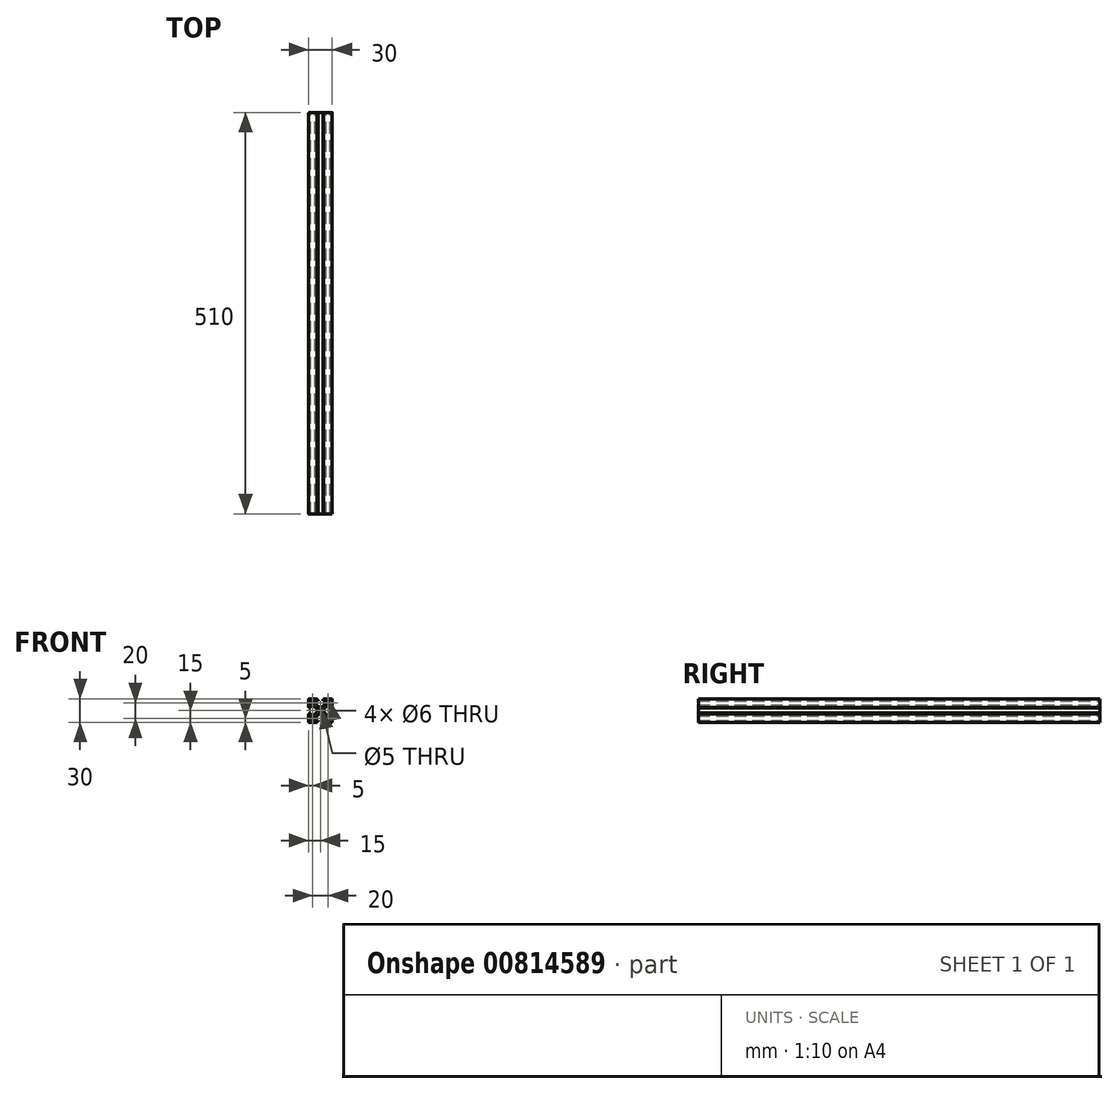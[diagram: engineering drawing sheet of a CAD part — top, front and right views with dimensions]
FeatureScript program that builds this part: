
annotation { "Feature Type Name" : "Feature", "Feature Type Description" : "" }
export const myFeature = defineFeature(function(context is Context, id is Id, definition is map)
    precondition{}
    {
        {
            var Q0;
            Q0=qCreatedBy(makeId("Front.planeOp"),FACE);
            var sketch = newSketch(context, id + "F0", { "sketchPlane" : qUnion([Q0])});
            skCircle(sketch, "E0", {"center": v(0, 0) * mm, "radius": 2.5 * mm});
            skCircle(sketch, "E1", {"center": v(-10, 10) * mm, "radius": 3 * mm});
            skCircle(sketch, "E2", {"center": v(10, 10) * mm, "radius": 3 * mm});
            skCircle(sketch, "E3", {"center": v(10, -10) * mm, "radius": 3 * mm});
            skCircle(sketch, "E4", {"center": v(-10, -10) * mm, "radius": 3 * mm});
            skLineSegment(sketch, "E5.bottom", {"start": v(-14, 15) * mm, "end": v(-4.5, 15) * mm});
            skLineSegment(sketch, "E5.top", {"start": v(-14, -15) * mm, "end": v(-4.2, -15) * mm});
            skLineSegment(sketch, "E5.left", {"start": v(-15, 14) * mm, "end": v(-15, 4.2) * mm});
            skLineSegment(sketch, "E5.right", {"start": v(15, 14) * mm, "end": v(15, 4.2) * mm});
            skPoint(sketch, "E6.visualSharp", {"position": v(-15, 15) * mm});
            skArc(sketch, "E6.filletArc", {"start": v(-14, 15) * mm, "mid": v(-14.7, 14.7) * mm, "end": v(-15, 14) * mm});
            skPoint(sketch, "E7.visualSharp", {"position": v(-15, -15) * mm});
            skArc(sketch, "E7.filletArc", {"start": v(-15, -14) * mm, "mid": v(-14.7, -14.7) * mm, "end": v(-14, -15) * mm});
            skPoint(sketch, "E8.visualSharp", {"position": v(15, -15) * mm});
            skArc(sketch, "E8.filletArc", {"start": v(14, -15) * mm, "mid": v(14.7, -14.7) * mm, "end": v(15, -14) * mm});
            skPoint(sketch, "E9.visualSharp", {"position": v(15, 15) * mm});
            skArc(sketch, "E9.filletArc", {"start": v(15, 14) * mm, "mid": v(14.7, 14.7) * mm, "end": v(14, 15) * mm});
            skLineSegment(sketch, "E10", {"start": v(-3.25, 13.7) * mm, "end": v(-3.25, 12.5) * mm});
            skLineSegment(sketch, "E11", {"start": v(-3.25, 12.5) * mm, "end": v(-5.25, 12.5) * mm});
            skLineSegment(sketch, "E12", {"start": v(-5.25, 12.5) * mm, "end": v(-5.25, 8) * mm});
            skLineSegment(sketch, "E13", {"start": v(-4.97, 7.3) * mm, "end": v(-2.54, 4.8) * mm});
            skLineSegment(sketch, "E14", {"start": v(-1.83, 4.5) * mm, "end": v(1.83, 4.5) * mm});
            skLineSegment(sketch, "E15", {"start": v(2.54, 4.8) * mm, "end": v(4.97, 7.3) * mm});
            skLineSegment(sketch, "E16", {"start": v(5.25, 8) * mm, "end": v(5.25, 12.5) * mm});
            skLineSegment(sketch, "E17", {"start": v(5.25, 12.5) * mm, "end": v(3.25, 12.5) * mm});
            skLineSegment(sketch, "E18", {"start": v(3.25, 12.5) * mm, "end": v(3.25, 13.7) * mm});
            skLineSegment(sketch, "E19.trimOffspring", {"start": v(4.5, 15) * mm, "end": v(14, 15) * mm});
            skPoint(sketch, "E20.visualSharp", {"position": v(-5.25, 7.6) * mm});
            skArc(sketch, "E20.filletArc", {"start": v(-5.25, 8) * mm, "mid": v(-5.18, 7.63) * mm, "end": v(-4.97, 7.3) * mm});
            skPoint(sketch, "E21.visualSharp", {"position": v(-2.25, 4.5) * mm});
            skArc(sketch, "E21.filletArc", {"start": v(-2.54, 4.8) * mm, "mid": v(-2.22, 4.58) * mm, "end": v(-1.83, 4.5) * mm});
            skPoint(sketch, "E22.visualSharp", {"position": v(2.25, 4.5) * mm});
            skArc(sketch, "E22.filletArc", {"start": v(1.83, 4.5) * mm, "mid": v(2.22, 4.58) * mm, "end": v(2.54, 4.8) * mm});
            skPoint(sketch, "E23.visualSharp", {"position": v(5.25, 7.6) * mm});
            skArc(sketch, "E23.filletArc", {"start": v(4.97, 7.3) * mm, "mid": v(5.18, 7.63) * mm, "end": v(5.25, 8) * mm});
            skLineSegment(sketch, "E24", {"start": v(-3.55, 14) * mm, "end": v(-3.7, 14) * mm});
            skLineSegment(sketch, "E25", {"start": v(-4.2, 14.5) * mm, "end": v(-4.2, 14.7) * mm});
            skLineSegment(sketch, "E26", {"start": v(3.55, 14) * mm, "end": v(3.7, 14) * mm});
            skLineSegment(sketch, "E27", {"start": v(4.2, 14.5) * mm, "end": v(4.2, 14.7) * mm});
            skPoint(sketch, "E28.visualSharp", {"position": v(-4.2, 15) * mm});
            skArc(sketch, "E28.filletArc", {"start": v(-4.2, 14.7) * mm, "mid": v(-4.29, 14.91) * mm, "end": v(-4.5, 15) * mm});
            skPoint(sketch, "E29.visualSharp", {"position": v(-3.25, 14) * mm});
            skArc(sketch, "E29.filletArc", {"start": v(-3.25, 13.7) * mm, "mid": v(-3.34, 13.91) * mm, "end": v(-3.55, 14) * mm});
            skPoint(sketch, "E30.visualSharp", {"position": v(3.25, 14) * mm});
            skArc(sketch, "E30.filletArc", {"start": v(3.55, 14) * mm, "mid": v(3.34, 13.91) * mm, "end": v(3.25, 13.7) * mm});
            skPoint(sketch, "E31.visualSharp", {"position": v(4.2, 15) * mm});
            skArc(sketch, "E31.filletArc", {"start": v(4.5, 15) * mm, "mid": v(4.29, 14.91) * mm, "end": v(4.2, 14.7) * mm});
            skPoint(sketch, "E32.visualSharp", {"position": v(4.2, 14) * mm});
            skArc(sketch, "E32.filletArc", {"start": v(3.7, 14) * mm, "mid": v(4.05, 14.15) * mm, "end": v(4.2, 14.5) * mm});
            skPoint(sketch, "E33.visualSharp", {"position": v(-4.2, 14) * mm});
            skArc(sketch, "E33.filletArc", {"start": v(-4.2, 14.5) * mm, "mid": v(-4.05, 14.15) * mm, "end": v(-3.7, 14) * mm});
            skPoint(sketch, "E34.1.0", {"position": v(-14, 3.25) * mm});
            skLineSegment(sketch, "E34.1.1", {"start": v(-12.5, -3.25) * mm, "end": v(-12.5, -5.25) * mm});
            skPoint(sketch, "E34.1.2", {"position": v(-15, 4.2) * mm});
            skPoint(sketch, "E34.1.3", {"position": v(-14, 4.2) * mm});
            skLineSegment(sketch, "E34.1.4", {"start": v(-12.5, -5.25) * mm, "end": v(-8, -5.25) * mm});
            skLineSegment(sketch, "E34.1.5", {"start": v(-4.8, 2.54) * mm, "end": v(-7.3, 4.97) * mm});
            skLineSegment(sketch, "E34.1.6", {"start": v(-12.5, 5.25) * mm, "end": v(-12.5, 3.25) * mm});
            skPoint(sketch, "E34.1.7", {"position": v(-15, -4.2) * mm});
            skPoint(sketch, "E34.1.8", {"position": v(-7.6, -5.25) * mm});
            skLineSegment(sketch, "E34.1.9", {"start": v(-8, 5.25) * mm, "end": v(-12.5, 5.25) * mm});
            skPoint(sketch, "E34.1.10", {"position": v(-14, -3.25) * mm});
            skPoint(sketch, "E34.1.11", {"position": v(-7.6, 5.25) * mm});
            skLineSegment(sketch, "E34.1.12", {"start": v(-4.5, -1.83) * mm, "end": v(-4.5, 1.83) * mm});
            skPoint(sketch, "E34.1.13", {"position": v(-4.5, 2.25) * mm});
            skPoint(sketch, "E34.1.14", {"position": v(-4.5, -2.25) * mm});
            skPoint(sketch, "E34.1.15", {"position": v(-14, -4.2) * mm});
            skLineSegment(sketch, "E34.1.16", {"start": v(-12.5, 3.25) * mm, "end": v(-13.7, 3.25) * mm});
            skLineSegment(sketch, "E34.1.17", {"start": v(-7.3, -4.97) * mm, "end": v(-4.8, -2.54) * mm});
            skLineSegment(sketch, "E34.1.18", {"start": v(-13.7, -3.25) * mm, "end": v(-12.5, -3.25) * mm});
            skArc(sketch, "E34.1.19", {"start": v(-14.5, -4.2) * mm, "mid": v(-14.15, -4.05) * mm, "end": v(-14, -3.7) * mm});
            skArc(sketch, "E34.1.20", {"start": v(-4.5, 1.83) * mm, "mid": v(-4.58, 2.22) * mm, "end": v(-4.8, 2.54) * mm});
            skArc(sketch, "E34.1.21", {"start": v(-8, -5.25) * mm, "mid": v(-7.63, -5.18) * mm, "end": v(-7.3, -4.97) * mm});
            skArc(sketch, "E34.1.22", {"start": v(-4.8, -2.54) * mm, "mid": v(-4.58, -2.22) * mm, "end": v(-4.5, -1.83) * mm});
            skArc(sketch, "E34.1.23", {"start": v(-7.3, 4.97) * mm, "mid": v(-7.63, 5.18) * mm, "end": v(-8, 5.25) * mm});
            skArc(sketch, "E34.1.24", {"start": v(-14, 3.55) * mm, "mid": v(-13.91, 3.34) * mm, "end": v(-13.7, 3.25) * mm});
            skLineSegment(sketch, "E34.1.25", {"start": v(-14, -3.55) * mm, "end": v(-14, -3.7) * mm});
            skArc(sketch, "E34.1.26", {"start": v(-14, 3.7) * mm, "mid": v(-14.15, 4.05) * mm, "end": v(-14.5, 4.2) * mm});
            skArc(sketch, "E34.1.27", {"start": v(-14.7, -4.2) * mm, "mid": v(-14.91, -4.29) * mm, "end": v(-15, -4.5) * mm});
            skArc(sketch, "E34.1.28", {"start": v(-13.7, -3.25) * mm, "mid": v(-13.91, -3.34) * mm, "end": v(-14, -3.55) * mm});
            skArc(sketch, "E34.1.29", {"start": v(-15, 4.5) * mm, "mid": v(-14.91, 4.29) * mm, "end": v(-14.7, 4.2) * mm});
            skLineSegment(sketch, "E34.1.30", {"start": v(-14.5, 4.2) * mm, "end": v(-14.7, 4.2) * mm});
            skLineSegment(sketch, "E34.1.31", {"start": v(-14.5, -4.2) * mm, "end": v(-14.7, -4.2) * mm});
            skLineSegment(sketch, "E34.1.32", {"start": v(-14, 3.55) * mm, "end": v(-14, 3.7) * mm});
            skPoint(sketch, "E34.2.0", {"position": v(-3.25, -14) * mm});
            skLineSegment(sketch, "E34.2.1", {"start": v(3.25, -12.5) * mm, "end": v(5.25, -12.5) * mm});
            skPoint(sketch, "E34.2.2", {"position": v(-4.2, -15) * mm});
            skPoint(sketch, "E34.2.3", {"position": v(-4.2, -14) * mm});
            skLineSegment(sketch, "E34.2.4", {"start": v(5.25, -12.5) * mm, "end": v(5.25, -8) * mm});
            skLineSegment(sketch, "E34.2.5", {"start": v(-2.54, -4.8) * mm, "end": v(-4.97, -7.3) * mm});
            skLineSegment(sketch, "E34.2.6", {"start": v(-5.25, -12.5) * mm, "end": v(-3.25, -12.5) * mm});
            skPoint(sketch, "E34.2.7", {"position": v(4.2, -15) * mm});
            skPoint(sketch, "E34.2.8", {"position": v(5.25, -7.6) * mm});
            skLineSegment(sketch, "E34.2.9", {"start": v(-5.25, -8) * mm, "end": v(-5.25, -12.5) * mm});
            skPoint(sketch, "E34.2.10", {"position": v(3.25, -14) * mm});
            skPoint(sketch, "E34.2.11", {"position": v(-5.25, -7.6) * mm});
            skLineSegment(sketch, "E34.2.12", {"start": v(1.83, -4.5) * mm, "end": v(-1.83, -4.5) * mm});
            skPoint(sketch, "E34.2.13", {"position": v(-2.25, -4.5) * mm});
            skPoint(sketch, "E34.2.14", {"position": v(2.25, -4.5) * mm});
            skPoint(sketch, "E34.2.15", {"position": v(4.2, -14) * mm});
            skLineSegment(sketch, "E34.2.16", {"start": v(-3.25, -12.5) * mm, "end": v(-3.25, -13.7) * mm});
            skLineSegment(sketch, "E34.2.17", {"start": v(4.97, -7.3) * mm, "end": v(2.54, -4.8) * mm});
            skLineSegment(sketch, "E34.2.18", {"start": v(3.25, -13.7) * mm, "end": v(3.25, -12.5) * mm});
            skArc(sketch, "E34.2.19", {"start": v(4.2, -14.5) * mm, "mid": v(4.05, -14.15) * mm, "end": v(3.7, -14) * mm});
            skArc(sketch, "E34.2.20", {"start": v(-1.83, -4.5) * mm, "mid": v(-2.22, -4.58) * mm, "end": v(-2.54, -4.8) * mm});
            skArc(sketch, "E34.2.21", {"start": v(5.25, -8) * mm, "mid": v(5.18, -7.63) * mm, "end": v(4.97, -7.3) * mm});
            skArc(sketch, "E34.2.22", {"start": v(2.54, -4.8) * mm, "mid": v(2.22, -4.58) * mm, "end": v(1.83, -4.5) * mm});
            skArc(sketch, "E34.2.23", {"start": v(-4.97, -7.3) * mm, "mid": v(-5.18, -7.63) * mm, "end": v(-5.25, -8) * mm});
            skArc(sketch, "E34.2.24", {"start": v(-3.55, -14) * mm, "mid": v(-3.34, -13.91) * mm, "end": v(-3.25, -13.7) * mm});
            skLineSegment(sketch, "E34.2.25", {"start": v(3.55, -14) * mm, "end": v(3.7, -14) * mm});
            skArc(sketch, "E34.2.26", {"start": v(-3.7, -14) * mm, "mid": v(-4.05, -14.15) * mm, "end": v(-4.2, -14.5) * mm});
            skArc(sketch, "E34.2.27", {"start": v(4.2, -14.7) * mm, "mid": v(4.29, -14.91) * mm, "end": v(4.5, -15) * mm});
            skArc(sketch, "E34.2.28", {"start": v(3.25, -13.7) * mm, "mid": v(3.34, -13.91) * mm, "end": v(3.55, -14) * mm});
            skArc(sketch, "E34.2.29", {"start": v(-4.5, -15) * mm, "mid": v(-4.29, -14.91) * mm, "end": v(-4.2, -14.7) * mm});
            skLineSegment(sketch, "E34.2.30", {"start": v(-4.2, -14.5) * mm, "end": v(-4.2, -14.7) * mm});
            skLineSegment(sketch, "E34.2.31", {"start": v(4.2, -14.5) * mm, "end": v(4.2, -14.7) * mm});
            skLineSegment(sketch, "E34.2.32", {"start": v(-3.55, -14) * mm, "end": v(-3.7, -14) * mm});
            skPoint(sketch, "E34.3.0", {"position": v(14, -3.25) * mm});
            skLineSegment(sketch, "E34.3.1", {"start": v(12.5, 3.25) * mm, "end": v(12.5, 5.25) * mm});
            skPoint(sketch, "E34.3.2", {"position": v(15, -4.2) * mm});
            skPoint(sketch, "E34.3.3", {"position": v(14, -4.2) * mm});
            skLineSegment(sketch, "E34.3.4", {"start": v(12.5, 5.25) * mm, "end": v(8, 5.25) * mm});
            skLineSegment(sketch, "E34.3.5", {"start": v(4.8, -2.54) * mm, "end": v(7.3, -4.97) * mm});
            skLineSegment(sketch, "E34.3.6", {"start": v(12.5, -5.25) * mm, "end": v(12.5, -3.25) * mm});
            skPoint(sketch, "E34.3.7", {"position": v(15, 4.2) * mm});
            skPoint(sketch, "E34.3.8", {"position": v(7.6, 5.25) * mm});
            skLineSegment(sketch, "E34.3.9", {"start": v(8, -5.25) * mm, "end": v(12.5, -5.25) * mm});
            skPoint(sketch, "E34.3.10", {"position": v(14, 3.25) * mm});
            skPoint(sketch, "E34.3.11", {"position": v(7.6, -5.25) * mm});
            skLineSegment(sketch, "E34.3.12", {"start": v(4.5, 1.83) * mm, "end": v(4.5, -1.83) * mm});
            skPoint(sketch, "E34.3.13", {"position": v(4.5, -2.25) * mm});
            skPoint(sketch, "E34.3.14", {"position": v(4.5, 2.25) * mm});
            skPoint(sketch, "E34.3.15", {"position": v(14, 4.2) * mm});
            skLineSegment(sketch, "E34.3.16", {"start": v(12.5, -3.25) * mm, "end": v(13.7, -3.25) * mm});
            skLineSegment(sketch, "E34.3.17", {"start": v(7.3, 4.97) * mm, "end": v(4.8, 2.54) * mm});
            skLineSegment(sketch, "E34.3.18", {"start": v(13.7, 3.25) * mm, "end": v(12.5, 3.25) * mm});
            skArc(sketch, "E34.3.19", {"start": v(14.5, 4.2) * mm, "mid": v(14.15, 4.05) * mm, "end": v(14, 3.7) * mm});
            skArc(sketch, "E34.3.20", {"start": v(4.5, -1.83) * mm, "mid": v(4.58, -2.22) * mm, "end": v(4.8, -2.54) * mm});
            skArc(sketch, "E34.3.21", {"start": v(8, 5.25) * mm, "mid": v(7.63, 5.18) * mm, "end": v(7.3, 4.97) * mm});
            skArc(sketch, "E34.3.22", {"start": v(4.8, 2.54) * mm, "mid": v(4.58, 2.22) * mm, "end": v(4.5, 1.83) * mm});
            skArc(sketch, "E34.3.23", {"start": v(7.3, -4.97) * mm, "mid": v(7.63, -5.18) * mm, "end": v(8, -5.25) * mm});
            skArc(sketch, "E34.3.24", {"start": v(14, -3.55) * mm, "mid": v(13.91, -3.34) * mm, "end": v(13.7, -3.25) * mm});
            skLineSegment(sketch, "E34.3.25", {"start": v(14, 3.55) * mm, "end": v(14, 3.7) * mm});
            skArc(sketch, "E34.3.26", {"start": v(14, -3.7) * mm, "mid": v(14.15, -4.05) * mm, "end": v(14.5, -4.2) * mm});
            skArc(sketch, "E34.3.27", {"start": v(14.7, 4.2) * mm, "mid": v(14.91, 4.29) * mm, "end": v(15, 4.5) * mm});
            skArc(sketch, "E34.3.28", {"start": v(13.7, 3.25) * mm, "mid": v(13.91, 3.34) * mm, "end": v(14, 3.55) * mm});
            skArc(sketch, "E34.3.29", {"start": v(15, -4.5) * mm, "mid": v(14.91, -4.29) * mm, "end": v(14.7, -4.2) * mm});
            skLineSegment(sketch, "E34.3.30", {"start": v(14.5, -4.2) * mm, "end": v(14.7, -4.2) * mm});
            skLineSegment(sketch, "E34.3.31", {"start": v(14.5, 4.2) * mm, "end": v(14.7, 4.2) * mm});
            skLineSegment(sketch, "E34.3.32", {"start": v(14, -3.55) * mm, "end": v(14, -3.7) * mm});
            skLineSegment(sketch, "E35.trimOffspring", {"start": v(-15, -4.2) * mm, "end": v(-15, -14) * mm});
            skLineSegment(sketch, "E36.trimOffspring", {"start": v(15, -4.2) * mm, "end": v(15, -14) * mm});
            skLineSegment(sketch, "E37.trimOffspring", {"start": v(4.2, -15) * mm, "end": v(14, -15) * mm});
            skSolve(sketch);
        }
        {
            var Q0;
            Q0=makeQuery(id+"F0.imprint","IMPRINT",FACE,{"disambiguationData":[TD([[makeQuery(id+"F0.imprint","IMPRINT",EDGE,{"derivedFrom":sQuery(id+"F0.wireOp",EDGE,"E0")}),-1.0]])]});
            extrude(context, id + "F1", {"entities" : qUnion([Q0]), "depth" : 510 * mm, "offsetDistance" : 25 * mm});
        }
    });
